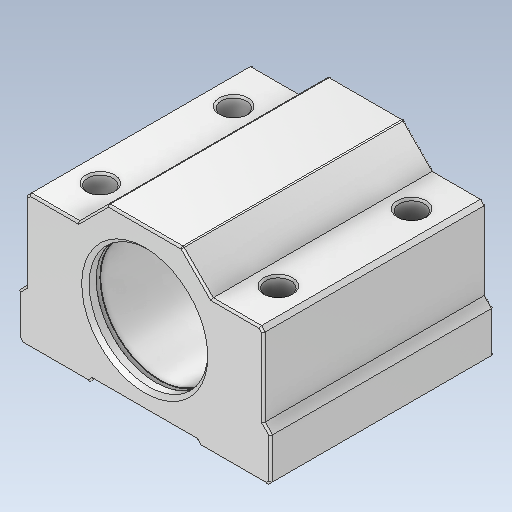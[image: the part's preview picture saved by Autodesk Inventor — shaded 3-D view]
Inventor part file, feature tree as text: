
AUTODESK INVENTOR PART (.ipt)
format: ipt  version: 2020.2 (Build 242310000, 310)  size: 369,664 bytes
history: native  units: mm
features: sketch x4, extrude x3, chamfer x3, other x2, revolve x1, fillet x1
ambient origin geometry x8: Origin, YZ Plane, XZ Plane, XY Plane, X Axis, Y Axis, Z Axis, Center Point
bodies: Body1 (feature_tree)
feature tree (14):
  other  "Bryła1"
  extrude  "Wyciągnięcie proste1"  Depth=22.0mm
  chamfer  "Faza1"  Distance=34.0mm
  other  "Płaszczyzna konstrukcyjna1"
  revolve  "Obrót1"
  extrude  "Wyciągnięcie proste2"  Depth=16.0mm
  extrude  "Wyciągnięcie proste3"  Depth=18.0mm
  chamfer  "Faza2"  Angle=135.0deg  [1 undecoded]
  fillet  "Zaokrąglenie1"  [1 undecoded]
  chamfer  "Faza3"  Distance=10.0mm
  sketch  "Szkic1"
  sketch  "Szkic2"
  sketch  "Szkic3"
  sketch  "Szkic4"
note: 2 required parameter values undecoded (feature->parameter linkage not recoverable at this tier; creation-order binding heuristic only, values carry confidence <= 0.55)
